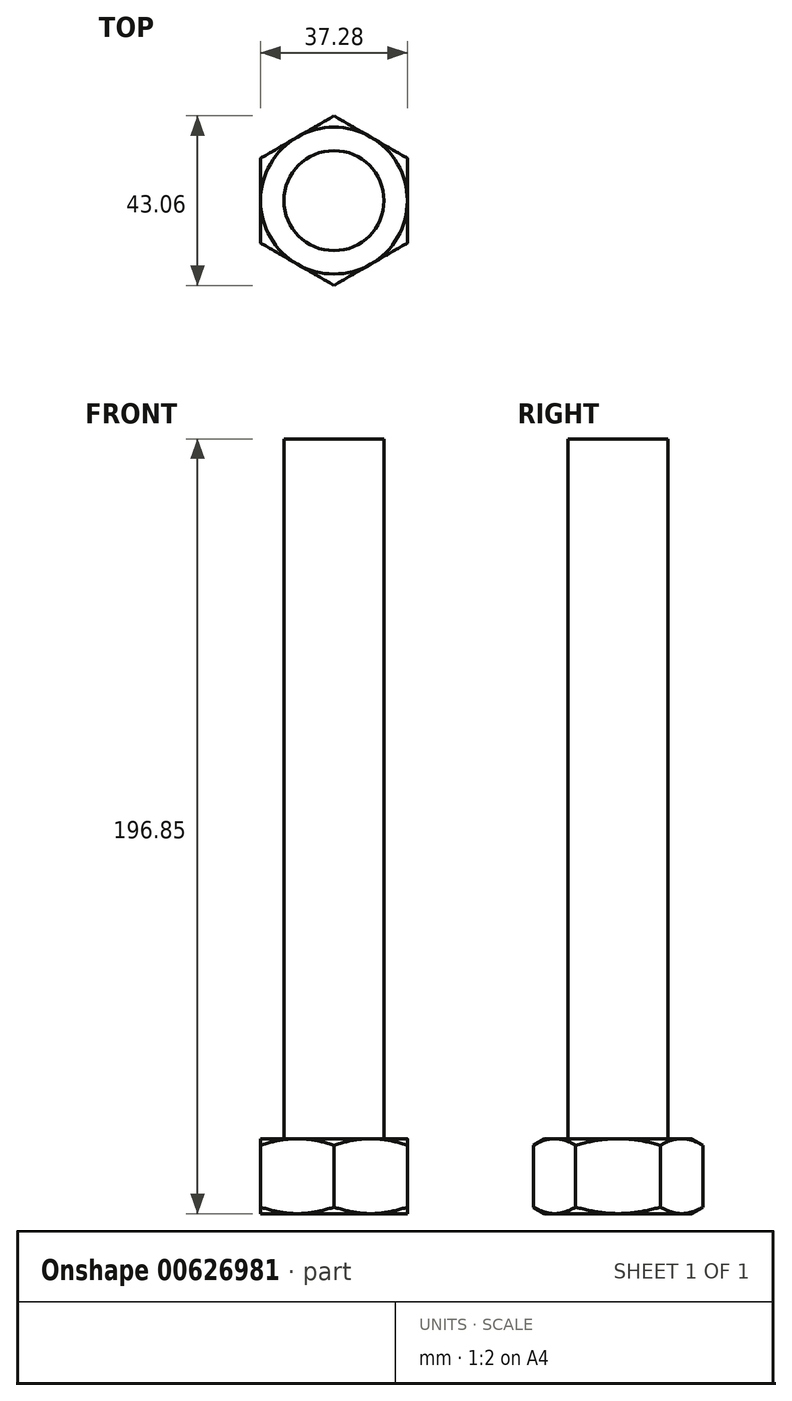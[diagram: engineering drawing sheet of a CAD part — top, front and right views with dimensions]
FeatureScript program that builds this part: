
annotation { "Feature Type Name" : "Feature", "Feature Type Description" : "" }
export const myFeature = defineFeature(function(context is Context, id is Id, definition is map)
    precondition{}
    {
        {
            var Q0;
            Q0=qCreatedBy(makeId("Top.planeOp"),FACE);
            var sketch = newSketch(context, id + "F0", { "sketchPlane" : qUnion([Q0])});
            skCircle(sketch, "E0", {"center": v(0, 0) * mm, "radius": 12.7 * mm});
            skSolve(sketch);
        }
        {
            var Q0;
            Q0 = qSketchRegion(id + "F0", true);
            extrude(context, id + "F1", {"entities" : qUnion([Q0]), "depth" : 177.8 * mm, "offsetDistance" : 25.4 * mm});
        }
        {
            var Q0;
            Q0=makeQuery(id+"F1.opExtrude","CAP_FACE",FACE,{"disambiguationData":[OSD([sQuery(id+"F0.wireOp",EDGE,"E0")])],"isStart":true});
            var sketch = newSketch(context, id + "F2", { "sketchPlane" : qUnion([Q0])});
            skCircle(sketch, "E1.cCircle", {"center": v(0, 0) * mm, "radius": 18.64 * mm, "construction": true});
            skLineSegment(sketch, "E1.0", {"start": v(18.64, -10.76) * mm, "end": v(0, -21.53) * mm});
            skLineSegment(sketch, "E1.1", {"start": v(0, -21.53) * mm, "end": v(-18.64, -10.76) * mm});
            skLineSegment(sketch, "E1.2", {"start": v(-18.64, -10.76) * mm, "end": v(-18.64, 10.76) * mm});
            skLineSegment(sketch, "E1.3", {"start": v(-18.64, 10.76) * mm, "end": v(0, 21.53) * mm});
            skLineSegment(sketch, "E1.4", {"start": v(0, 21.53) * mm, "end": v(18.64, 10.76) * mm});
            skLineSegment(sketch, "E1.5", {"start": v(18.64, 10.76) * mm, "end": v(18.64, -10.76) * mm});
            skPoint(sketch, "E1.0.midPoint", {"position": v(9.32, -16.15) * mm});
            skSolve(sketch);
        }
        {
            var Q0;
            Q0=makeQuery(id+"F2.imprint","IMPRINT",FACE,{"disambiguationData":[TD([[makeQuery(id+"F2.imprint","IMPRINT",EDGE,{"derivedFrom":sQuery(id+"F2.wireOp",EDGE,"E1.0")}),-1.0]])]});
            var Q1;
            Q1=makeQuery(id+"F2.imprint","IMPRINT",FACE,{"disambiguationData":[TD([[makeQuery(id+"F2.imprint","IMPRINT",EDGE,{"derivedFrom":makeQuery(id+"F1.opExtrude","CAP_EDGE",EDGE,{"disambiguationData":[OSD([sQuery(id+"F0.wireOp",EDGE,"E0")])],"isStart":true})}),-1.0]])]});
            extrude(context, id + "F3", {"entities" : qUnion([Q0, Q1]), "operationType" : NewBodyOperationType.ADD, "depth" : 19.05 * mm, "offsetDistance" : 25.4 * mm});
        }
        {
            var Q0;
            Q0=qCreatedBy(makeId("Front.planeOp"),FACE);
            var sketch = newSketch(context, id + "F4", { "sketchPlane" : qUnion([Q0])});
            skPoint(sketch, "E2.0", {"position": v(0, 0) * mm});
            skPoint(sketch, "E3.0", {"position": v(0, -19.05) * mm});
            skPoint(sketch, "E4.0", {"position": v(18.64, -9.53) * mm});
            skLineSegment(sketch, "E5", {"start": v(0, 0) * mm, "end": v(0, -19.05) * mm, "construction": true});
            skLineSegment(sketch, "E6", {"start": v(0, -9.53) * mm, "end": v(18.64, -9.53) * mm, "construction": true});
            skLineSegment(sketch, "E7", {"start": v(18.64, -19.05) * mm, "end": v(31.38, -19.05) * mm});
            skLineSegment(sketch, "E8", {"start": v(31.38, -19.05) * mm, "end": v(31.38, -11.7) * mm});
            skLineSegment(sketch, "E9", {"start": v(31.38, -11.7) * mm, "end": v(18.64, -19.05) * mm});
            skLineSegment(sketch, "E10.MirrorCS", {"start": v(31.38, -7.35) * mm, "end": v(18.64, 0) * mm});
            skLineSegment(sketch, "E11.MirrorCS", {"start": v(18.64, 0) * mm, "end": v(31.38, 0) * mm});
            skLineSegment(sketch, "E12.MirrorCS", {"start": v(31.38, 0) * mm, "end": v(31.38, -7.35) * mm});
            skSolve(sketch);
        }
        {
            var Q0;
            Q0=makeQuery(id+"F4.imprint","IMPRINT",FACE,{"disambiguationData":[TD([[makeQuery(id+"F4.imprint","IMPRINT",EDGE,{"derivedFrom":sQuery(id+"F4.wireOp",EDGE,"E7")}),1.0]])]});
            var Q1;
            Q1=makeQuery(id+"F4.imprint","IMPRINT",FACE,{"disambiguationData":[TD([[makeQuery(id+"F4.imprint","IMPRINT",EDGE,{"derivedFrom":sQuery(id+"F4.wireOp",EDGE,"E10.MirrorCS")}),-1.0]])]});
            var Q2;
            Q2=sQuery(id+"F4.wireOp",EDGE,"E5");
            revolve(context, id + "F5", {"operationType" : NewBodyOperationType.REMOVE, "entities" : qUnion([Q0, Q1]), "axis" : qUnion([Q2]), "revolveType" : RevolveType.FULL, "oppositeDirection" : true});
        }
    });
